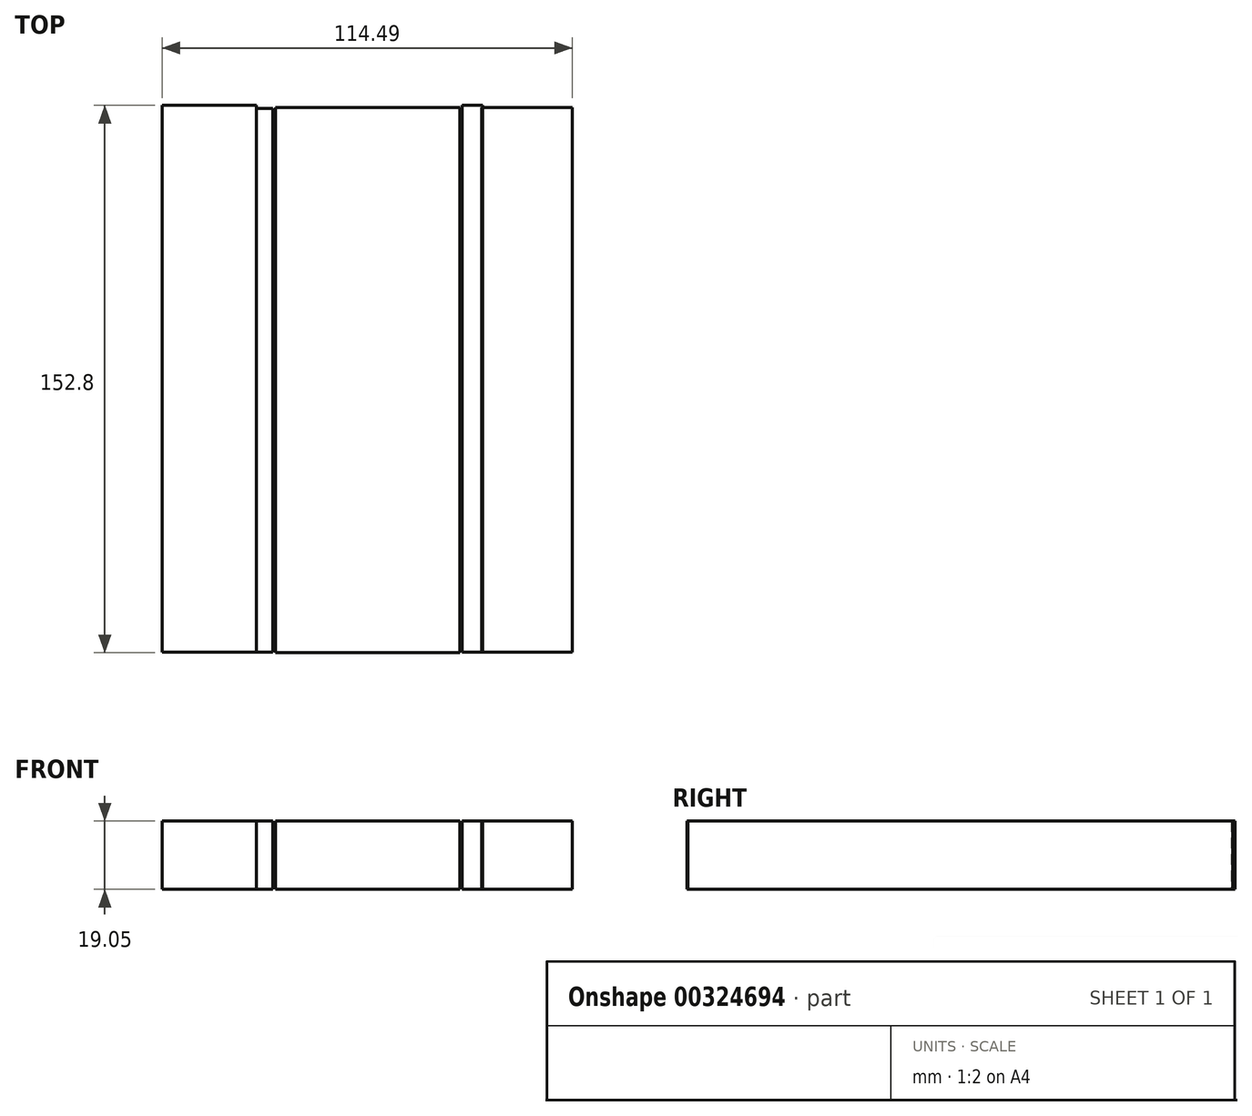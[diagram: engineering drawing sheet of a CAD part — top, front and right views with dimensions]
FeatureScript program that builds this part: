
annotation { "Feature Type Name" : "Feature", "Feature Type Description" : "" }
export const myFeature = defineFeature(function(context is Context, id is Id, definition is map)
    precondition{}
    {
        {
            var Q0;
            Q0=qCreatedBy(makeId("Top.planeOp"),FACE);
            var sketch = newSketch(context, id + "F0", { "sketchPlane" : qUnion([Q0])});
            skLineSegment(sketch, "E0.bottom", {"start": v(-27.56, 75.75) * mm, "end": v(23.89, 75.75) * mm});
            skLineSegment(sketch, "E0.top", {"start": v(-27.56, -76.45) * mm, "end": v(23.89, -76.45) * mm});
            skLineSegment(sketch, "E0.left", {"start": v(-27.56, 75.75) * mm, "end": v(-27.56, -76.45) * mm});
            skLineSegment(sketch, "E0.right", {"start": v(23.89, 75.75) * mm, "end": v(23.89, -76.45) * mm});
            skSolve(sketch);
        }
        {
            var Q0;
            Q0=makeQuery(id+"F0.imprint","IMPRINT",FACE,{"disambiguationData":[TD([[makeQuery(id+"F0.imprint","IMPRINT",EDGE,{"derivedFrom":sQuery(id+"F0.wireOp",EDGE,"E0.bottom")}),-1.0]])]});
            extrude(context, id + "F1", {"entities" : qUnion([Q0]), "depth" : 19.05 * mm});
        }
        {
            var Q0;
            Q0=qCreatedBy(makeId("Top.planeOp"),FACE);
            var sketch = newSketch(context, id + "F2", { "sketchPlane" : qUnion([Q0])});
            skLineSegment(sketch, "E1.bottom", {"start": v(-28.4, 75.44) * mm, "end": v(-32.97, 75.44) * mm});
            skLineSegment(sketch, "E1.top", {"start": v(-28.4, -76.3) * mm, "end": v(-32.97, -76.3) * mm});
            skLineSegment(sketch, "E1.left", {"start": v(-28.4, 75.44) * mm, "end": v(-28.4, -76.3) * mm});
            skLineSegment(sketch, "E1.right", {"start": v(-32.97, 75.44) * mm, "end": v(-32.97, -76.3) * mm});
            skLineSegment(sketch, "E2.bottom", {"start": v(24.42, 76.35) * mm, "end": v(30.22, 76.35) * mm});
            skLineSegment(sketch, "E2.top", {"start": v(24.42, -76.3) * mm, "end": v(30.22, -76.3) * mm});
            skLineSegment(sketch, "E2.left", {"start": v(24.42, 76.35) * mm, "end": v(24.42, -76.3) * mm});
            skLineSegment(sketch, "E2.right", {"start": v(30.22, 76.35) * mm, "end": v(30.22, -76.3) * mm});
            skSolve(sketch);
        }
        {
            var Q0;
            Q0=makeQuery(id+"F2.imprint","IMPRINT",FACE,{"disambiguationData":[TD([[makeQuery(id+"F2.imprint","IMPRINT",EDGE,{"derivedFrom":sQuery(id+"F2.wireOp",EDGE,"E1.bottom")}),1.0]])]});
            var Q1;
            Q1=makeQuery(id+"F2.imprint","IMPRINT",FACE,{"disambiguationData":[TD([[makeQuery(id+"F2.imprint","IMPRINT",EDGE,{"derivedFrom":sQuery(id+"F2.wireOp",EDGE,"E2.bottom")}),-1.0]])]});
            extrude(context, id + "F3", {"entities" : qUnion([Q0, Q1]), "depth" : 19.05 * mm});
        }
        {
            var Q0;
            Q0=qCreatedBy(makeId("Top.planeOp"),FACE);
            var sketch = newSketch(context, id + "F4", { "sketchPlane" : qUnion([Q0])});
            skLineSegment(sketch, "E3.bottom", {"start": v(-32.97, 76.35) * mm, "end": v(-59.23, 76.35) * mm});
            skLineSegment(sketch, "E3.top", {"start": v(-32.97, -76.3) * mm, "end": v(-59.23, -76.3) * mm});
            skLineSegment(sketch, "E3.left", {"start": v(-32.97, 76.35) * mm, "end": v(-32.97, -76.3) * mm});
            skLineSegment(sketch, "E3.right", {"start": v(-59.23, 76.35) * mm, "end": v(-59.23, -76.3) * mm});
            skLineSegment(sketch, "E4.bottom", {"start": v(29.92, 75.74) * mm, "end": v(55.26, 75.74) * mm});
            skLineSegment(sketch, "E4.top", {"start": v(29.92, -76.3) * mm, "end": v(55.26, -76.3) * mm});
            skLineSegment(sketch, "E4.left", {"start": v(29.92, 75.74) * mm, "end": v(29.92, -76.3) * mm});
            skLineSegment(sketch, "E4.right", {"start": v(55.26, 75.74) * mm, "end": v(55.26, -76.3) * mm});
            skSolve(sketch);
        }
        {
            var Q0;
            Q0=makeQuery(id+"F4.imprint","IMPRINT",FACE,{"disambiguationData":[TD([[makeQuery(id+"F4.imprint","IMPRINT",EDGE,{"derivedFrom":sQuery(id+"F4.wireOp",EDGE,"E3.bottom")}),1.0]])]});
            var Q1;
            Q1=makeQuery(id+"F4.imprint","IMPRINT",FACE,{"disambiguationData":[TD([[makeQuery(id+"F4.imprint","IMPRINT",EDGE,{"derivedFrom":sQuery(id+"F4.wireOp",EDGE,"E4.bottom")}),-1.0]])]});
            extrude(context, id + "F5", {"entities" : qUnion([Q0, Q1]), "depth" : 19.05 * mm});
        }
    });
